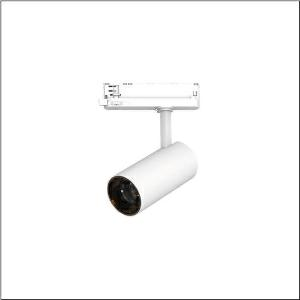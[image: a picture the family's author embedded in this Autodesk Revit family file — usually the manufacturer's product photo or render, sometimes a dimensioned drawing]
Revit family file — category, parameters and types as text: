
# Revit family: spot_31_slim_51sf137fa2b
name_source: partatom
category: Lighting Fixtures
units: mm (PartAtom-declared; Revit-internal decimal feet)

## family parameters
Cut with Voids When Loaded = No
Host = Face
Light Source = No
Part Type = Normal
Room Calculation Point = No
Round Connector Dimension = Use Diameter
Shared = No

## types (1)
- Spot 31 Slim (1 x LED, 2150 lm, 17.6 W, 2700K)
    Apparent Load = 18 VA
    CIE Flux Codes = 97 100 100 100 100
    Color Rendering = 90
    Color Temperature = 2700K
    Default Elevation = 1800 mm
    Description = Spot 31 Slim, directional spotlight, light control with reflector, of aluminium, LED rated luminous flux: 2.150lm, light colour: 927, control gear: ECG, with 3-phase adapter, mains connection: 220..240V, AC, 50/60Hz, housing, of aluminium, traffic white (RAL 9016), diameter: 70mm, adapter, of plastic, protection rating (complete): IP20, insulation class (complete): insulation class I (protective earthing), certification: CE, impact resistance: IK02, packaging unit: 1 piece
    Height = 210 mm
    Lamp = 1 x LED
    Lamp Light Flux = 2150 lm
    Lamp Power = 17.6 W
    Lamp count = 1
    Length = 70 mm
    Luminous efficacy = 122 lm/W
    Manufacturer = Siteco
    ModVariant = No
    Model = 51SF137FA2B
    Mounting Place = Ceiling
    Mounting Type = Pendant
    Number of Poles = 1
    OnlyDefault = Yes
    Power Factor = 1
    Product Name = Spot 31 Slim
    Product group = directional spotlight
    ProductGroupID = 905
    Protection Class = Protection class I
    Protection Degree = IP 20
    RLX_Detail_Level = 1
    RLX_Emergency_Light_Flux = 0 lm
    RLX_Emergency_Type = 0
    RLX_Emergency_Type_DB = No
    RlxData = <blob elided: 14145 chars, md5=b04df9e9>
    Socket = socket
    Standby Power = 0 W
    System Light Flux = 2150 lm
    System Power = 18 W
    Type Comments = Product without accessories
    Type Image = l_1228468.jpg
    URL = http://relux.com
    VarID = ---
    Voltage = 0 V
    Weight = 0.00 kg
    Width = 0 mm  [stored 0 ft]

note: [stored X ft] marks values corroborated as IEEE doubles in the binary element streams (Revit-internal decimal feet)

## geometry (parser evidence)
native form markers: Sweep x10
no freeform markers — native parametric forms only
